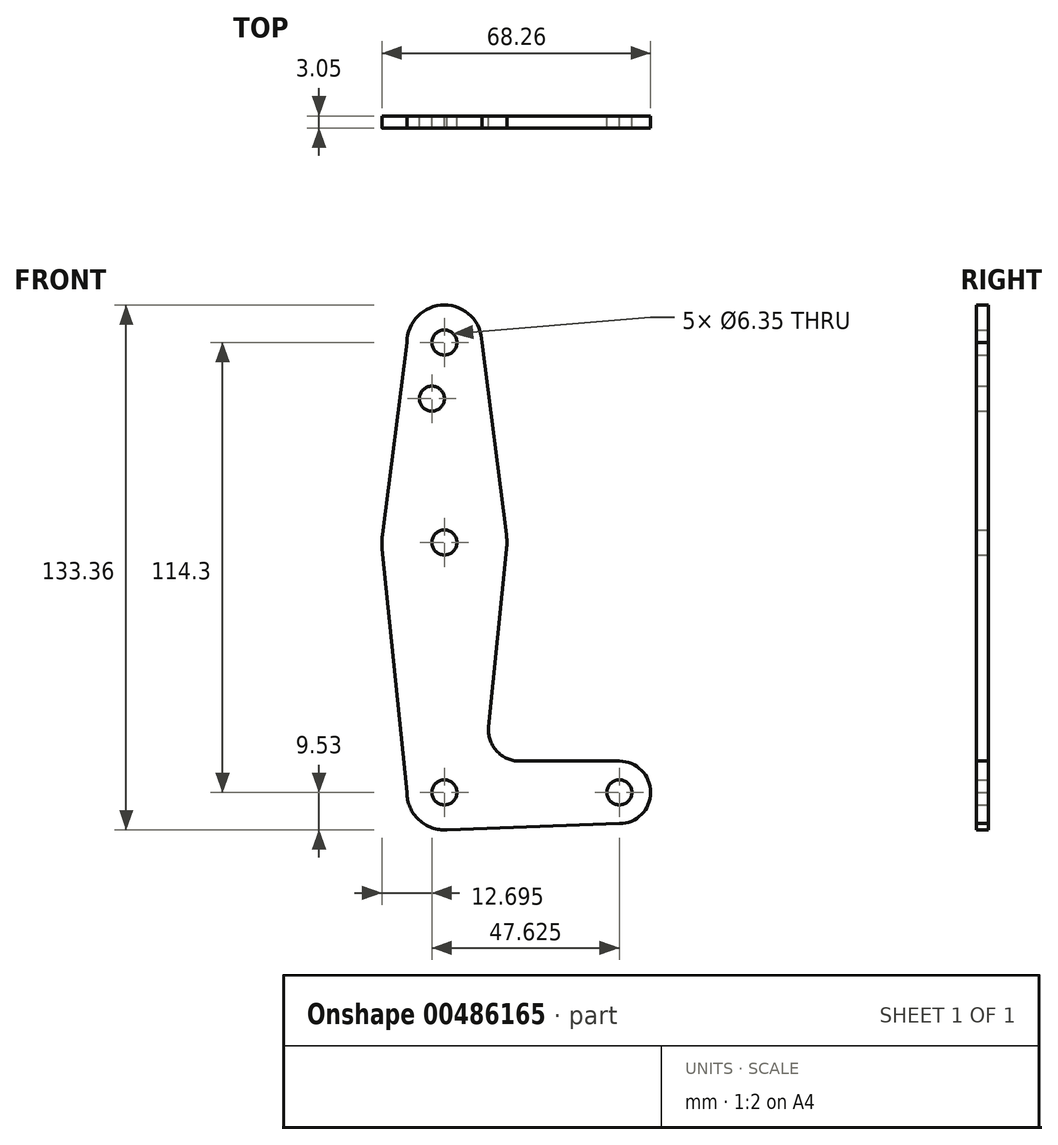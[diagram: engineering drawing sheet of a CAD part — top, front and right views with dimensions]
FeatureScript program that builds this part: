
annotation { "Feature Type Name" : "Feature", "Feature Type Description" : "" }
export const myFeature = defineFeature(function(context is Context, id is Id, definition is map)
    precondition{}
    {
        {
            var Q0;
            Q0=qCreatedBy(makeId("Front.planeOp"),FACE);
            var sketch = newSketch(context, id + "F0", { "sketchPlane" : qUnion([Q0])});
            skLineSegment(sketch, "E0", {"start": v(0, 0) * mm, "end": v(0, 114.3) * mm, "construction": true});
            skLineSegment(sketch, "E1", {"start": v(0, 0) * mm, "end": v(44.45, 0) * mm, "construction": true});
            skCircle(sketch, "E2", {"center": v(0, 114.3) * mm, "radius": 9.53 * mm});
            skCircle(sketch, "E3", {"center": v(44.45, 0) * mm, "radius": 7.94 * mm});
            skCircle(sketch, "E4", {"center": v(0, 63.5) * mm, "radius": 15.88 * mm});
            skCircle(sketch, "E5", {"center": v(0, 0) * mm, "radius": 9.53 * mm});
            skLineSegment(sketch, "E6", {"start": v(0, -9.53) * mm, "end": v(44.45, -7.94) * mm});
            skLineSegment(sketch, "E7", {"start": v(44.45, 7.94) * mm, "end": v(19.12, 7.94) * mm});
            skLineSegment(sketch, "E8", {"start": v(9.52, 114.3) * mm, "end": v(15.75, 65.5) * mm});
            skLineSegment(sketch, "E9", {"start": v(-9.53, 114.3) * mm, "end": v(-15.75, 65.5) * mm});
            skLineSegment(sketch, "E10", {"start": v(-15.8, 61.9) * mm, "end": v(-9.52, 0) * mm});
            skLineSegment(sketch, "E11", {"start": v(15.8, 61.9) * mm, "end": v(11.22, 16.69) * mm});
            skCircle(sketch, "E12", {"center": v(0, 114.3) * mm, "radius": 3.18 * mm});
            skCircle(sketch, "E13", {"center": v(0, 63.5) * mm, "radius": 3.18 * mm});
            skCircle(sketch, "E14", {"center": v(0, 0) * mm, "radius": 3.18 * mm});
            skCircle(sketch, "E15", {"center": v(44.45, 0) * mm, "radius": 3.18 * mm});
            skArc(sketch, "E16.filletArc", {"start": v(11.22, 16.69) * mm, "mid": v(13.23, 10.56) * mm, "end": v(19.12, 7.94) * mm});
            skCircle(sketch, "E17", {"center": v(-3.17, 100.03) * mm, "radius": 3.18 * mm});
            skSolve(sketch);
        }
        {
            var Q0;
            Q0 = qSketchRegion(id + "F0", true);
            extrude(context, id + "F1", {"entities" : qUnion([Q0]), "depth" : 3.05 * mm});
        }
    });
